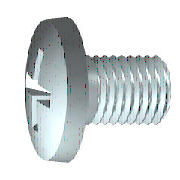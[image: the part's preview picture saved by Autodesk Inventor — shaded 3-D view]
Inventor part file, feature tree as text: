
AUTODESK INVENTOR PART (.ipt)
format: ipt  version: 2015 (Build 190159000, 159)  size: 237,568 bytes
history: native  units: mm (DEFAULTED — no unit token found)
features: chamfer x4, other x3, sketch x2, revolve x1, fillet x1, extrude x1, pattern_circular x1
ambient origin geometry x8: Origin, YZ Plane, XZ Plane, XY Plane, X Axis, Y Axis, Z Axis, Center Point
bodies: Solid1 (feature_tree)
feature tree (13):
  revolve  "Revolution1"  [1 undecoded]
  chamfer  "Chamfer1"  Distance=0.125mm
  chamfer  "Chamfer2"  Distance=0.125mm
  fillet  "Fillet1"  Radius=0.25mm
  extrude  "Extrusion1"  Depth=10.0mm
  pattern_circular  "PolarArray1"  [2 undecoded]
  chamfer  "Chamfer3"  Distance=1.612mm
  chamfer  "Chamfer4"  Distance=0.62mm
  other  "MSC_A1"
  other  "MSC_PF1"
  other  "MSC_PT1"
  sketch  "Sketch2"  dims[d6=2.75mm d9=0.872665mm]
  sketch  "Sketch3"  dims[d10=90.0deg d11=0.125mm d12=0.125mm d13=0.25mm d14=0.25mm d16=10.0mm d17=0.0mm d19=1.612mm d20=0.62mm d21=2.52mm d22=0.516667mm d23=0.0mm d24=40.0mm d26=360.0deg d28=0.0mm d29=0.0mm d30=0.442857mm d31=0.442857mm d32=0.206667mm d33=0.206667mm d34=45.0deg d35=45.0deg d36=45.0deg d37=45.0deg d38=0.0mm d39=0.0mm d40=0.0mm]
note: 3 required parameter values undecoded (feature->parameter linkage not recoverable at this tier; creation-order binding heuristic only, values carry confidence <= 0.55)